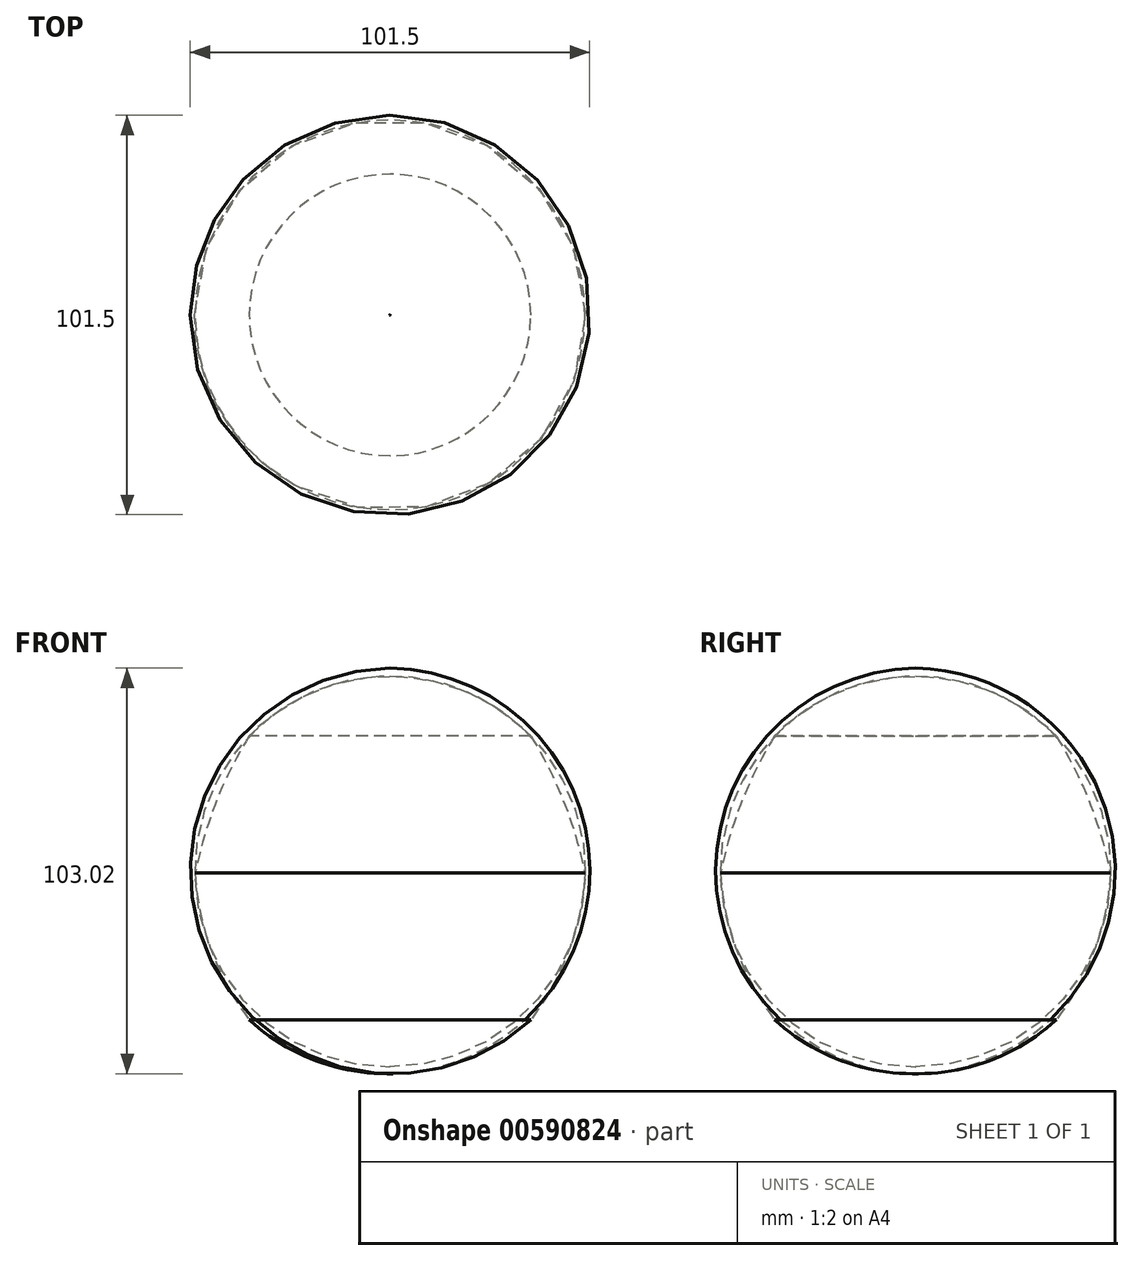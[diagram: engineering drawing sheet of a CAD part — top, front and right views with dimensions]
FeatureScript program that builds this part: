
annotation { "Feature Type Name" : "Feature", "Feature Type Description" : "" }
export const myFeature = defineFeature(function(context is Context, id is Id, definition is map)
    precondition{}
    {
        {
            var Q0;
            Q0=qCreatedBy(makeId("Front.planeOp"),FACE);
            var sketch = newSketch(context, id + "F0", { "sketchPlane" : qUnion([Q0])});
            skLineSegment(sketch, "E0", {"start": v(0, 50.08) * mm, "end": v(0, -50.96) * mm});
            skArc(sketch, "E1", {"start": v(35.77, 34.9) * mm, "mid": v(19.43, 46.13) * mm, "end": v(0, 50.08) * mm});
            skArc(sketch, "E2", {"start": v(49.5, 0) * mm, "mid": v(44.18, 18.05) * mm, "end": v(35.77, 34.9) * mm});
            skArc(sketch, "E3", {"start": v(0, -50.96) * mm, "mid": v(19.2, -47.54) * mm, "end": v(35.77, -37.23) * mm});
            skArc(sketch, "E4", {"start": v(35.77, -37.23) * mm, "mid": v(45.41, -19.64) * mm, "end": v(49.5, 0) * mm});
            skSolve(sketch);
        }
        {
            var Q0;
            Q0 = qSketchRegion(id + "F0", true);
            var Q1;
            Q1=sQuery(id+"F0.wireOp",EDGE,"E0");
            revolve(context, id + "F1", {"entities" : qUnion([Q0]), "axis" : qUnion([Q1]), "revolveType" : RevolveType.FULL});
        }
    });
